# Revit family: RN 85212 Optiflex-Profix-Set di collegamento
name_source: partatom
category: HLS-Bauteile
units: mm (PartAtom-declared; Revit-internal decimal feet)

## family parameters
Arbeitsebenenbasiert = Nein
Beim Laden mit Abzugskörper schneiden = Nein
Bemaßung runder Anschluss = Durchmesser verwenden
Gemeinsam genutzt = Nein
Immer vertikal = Ja
Klassifizierung = Keine
Raumberechnungspunkt = Nein
Teiletyp = Normal

## types (2) — shared parameters
1.010.00.2 Blattnummer der Richtlinie = 29
1.010.00.3 Ausgabedatum (Monat) der Richtlinie = 201308
1.010.00.4 Herstellername = R. Nussbaum AG
1.010.00.5 Revisionsdatum der Datei = 20190521
1.010.00.6 Webadresse des Herstellers = http://www.nussbaum.ch
1.100.00.4 Produktbezeichnung = Versorgung
1.110.00.2 Index = 5
1.110.00.4 Produktbezeichnung = Optiflex
1.960/3L.00.8 Link (URL) = https://www.nussbaum.ch
29.700.00.4 Produktname = Optiflex-Profix-Anschluss-Set, für Bad und Dusche
29.700.00.5 Produktkennung = 2
29.700.00.6 Querschnittsform = 1
29.700.00.7 Nennweitensystem = DN
29.700.00.8 Nenndrucksystem = PN
29.710.02.4 Nenndruck = 10
29.710.02.5 max. zul. Überdruck [hPa] = 1000
29.710.02.7 max. zul. Dauer-Betriebsdruck [hPa] = 1000
29.710.02.9 max. zul. Dauer-Betriebstemperatur [°C] = 70
CONNECTOR0_dZ_00 = 106 mm
CONNECTOR0_dZ_01 = 72 mm
CONNECTOR0_ref_dX = 77 mm
CONNECTOR0_ref_dY = 24 mm
CONNECTOR0_ref_dZ = 72 mm
CONNECTOR1_dZ_00 = 106 mm
CONNECTOR1_dZ_01 = 72 mm
CONNECTOR1_ref_dX = 77 mm
CONNECTOR1_ref_dY = 24 mm
CONNECTOR1_ref_dZ = 72 mm
CONNECTOR2_DIAMETER_dY_0r = 15 mm
CONNECTOR2_dY_00 = 25 mm  [stored 0.082021 ft]
CONNECTOR2_dY_01 = 12 mm  [stored 0.0393701 ft]
CONNECTOR2_ref_dX = 77 mm
CONNECTOR2_ref_dY = 12 mm  [stored 0.0393701 ft]
CONNECTOR3_DIAMETER_dY_0r = 15 mm
CONNECTOR3_dY_00 = 25 mm  [stored 0.082021 ft]
CONNECTOR3_dY_01 = 12 mm  [stored 0.0393701 ft]
CONNECTOR3_ref_dX = 77 mm
CONNECTOR3_ref_dY = 12 mm  [stored 0.0393701 ft]
Connector Visibility = Nein
EnclosingSpace Visibility = Nein
Hersteller = R. Nussbaum AG
URL = https://www.nussbaum.ch

## per-type parameters (varying)
| type | 1.800.00.3 TGA-Nummer | 1.800.00.4 Kommentarfeld | 1.810.00.3 Hersteller-Bestellnummer | 1.810.00.4 DATANORM-Nummer | 1.810.00.5 StLB-Nummer | 1.810.00.6 GTIN-Nummer | 29.710.02.10 Formstück-Gewicht [kg] | 29.710.02.3 Benennung | CONNECTOR0_DIAMETER_dZ_0r | CONNECTOR1_DIAMETER_dZ_0r | Modell | R. Nussbaum AG 85212.21 de Visibility | R. Nussbaum AG 85212.22 de Visibility | Typenkommentare |
| DN=15 | 01900500000000000000000000000000000000000000000067???000000000000002 | 85212.22, Optiflex-Profix-Anschluss-Set, für Bad und Dusche, DN=15, L=153, Rp=½ | 85212.22 | 85212.22 | 322.612 | 7612945744357 | 0.962 | Optiflex-Profix-Anschluss-Set, für Bad und Dusche, DN=15, L=153, Rp=½ | 15 mm | 15 mm | 85212.22 | Nein | Ja | Optiflex-Profix-Set di collegamento  DN=15 |
| DN=12 | 01900500000000000000000000000000000000000000000067???000000000000001 | 85212.21, Optiflex-Profix-Anschluss-Set, für Bad und Dusche, DN=12, L=153, Rp=½ | 85212.21 | 85212.21 | 322.611 | 7612945744340 | 0.95 | Optiflex-Profix-Anschluss-Set, für Bad und Dusche, DN=12, L=153, Rp=½ | 12 mm  [stored 0.0393701 ft] | 12 mm  [stored 0.0393701 ft] | 85212.21 | Ja | Nein | Optiflex-Profix-Set di collegamento  DN=12 |

note: [stored X ft] marks values corroborated as IEEE doubles in the binary element streams (Revit-internal decimal feet)

## geometry (parser evidence)
native form markers: Sweep x3
no freeform markers — native parametric forms only
